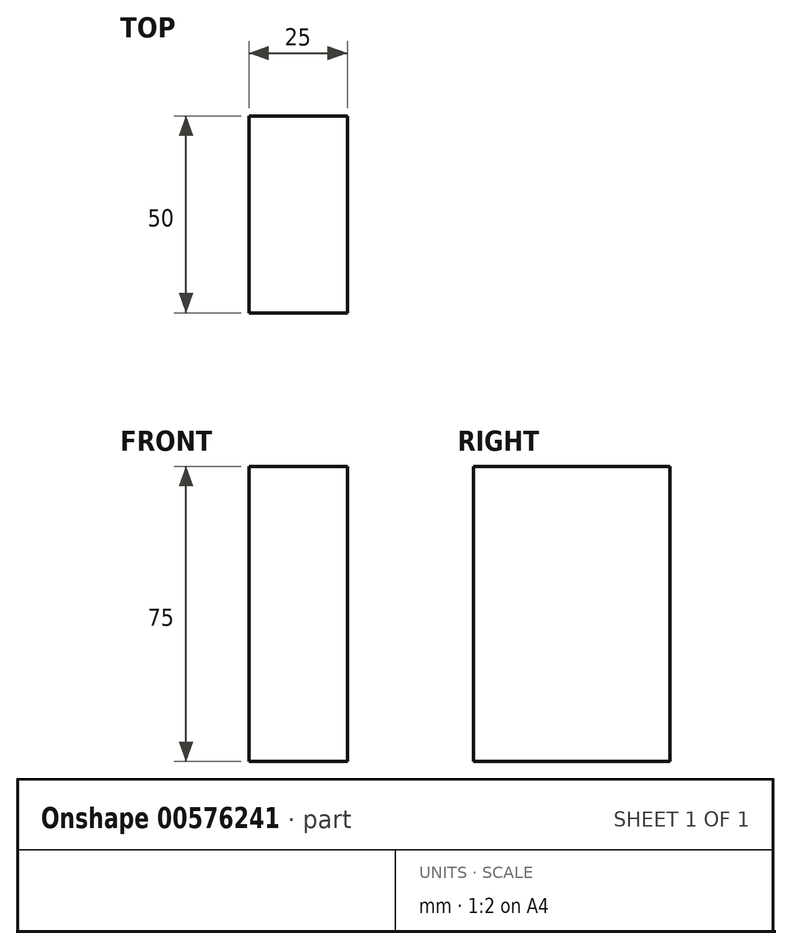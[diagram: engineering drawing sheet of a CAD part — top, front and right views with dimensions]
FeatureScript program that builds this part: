
annotation { "Feature Type Name" : "Feature", "Feature Type Description" : "" }
export const myFeature = defineFeature(function(context is Context, id is Id, definition is map)
    precondition{}
    {
        {
            var Q0;
            Q0=qCreatedBy(makeId("Top.planeOp"),FACE);
            var sketch = newSketch(context, id + "F0", { "sketchPlane" : qUnion([Q0])});
            skLineSegment(sketch, "E0.bottom", {"start": v(-18.22, 38.33) * mm, "end": v(6.78, 38.33) * mm});
            skLineSegment(sketch, "E0.top", {"start": v(-18.22, -11.67) * mm, "end": v(6.78, -11.67) * mm});
            skLineSegment(sketch, "E0.left", {"start": v(-18.22, 38.33) * mm, "end": v(-18.22, -11.67) * mm});
            skLineSegment(sketch, "E0.right", {"start": v(6.78, 38.33) * mm, "end": v(6.78, -11.67) * mm});
            skSolve(sketch);
        }
        {
            var Q0;
            Q0=makeQuery(id+"F0.imprint","IMPRINT",FACE,{"disambiguationData":[TD([[makeQuery(id+"F0.imprint","IMPRINT",EDGE,{"derivedFrom":sQuery(id+"F0.wireOp",EDGE,"E0.bottom")}),-1.0]])]});
            extrude(context, id + "F1", {"entities" : qUnion([Q0]), "endBound" : BoundingType.SYMMETRIC, "depth" : 75 * mm, "offsetDistance" : 25 * mm});
        }
    });
